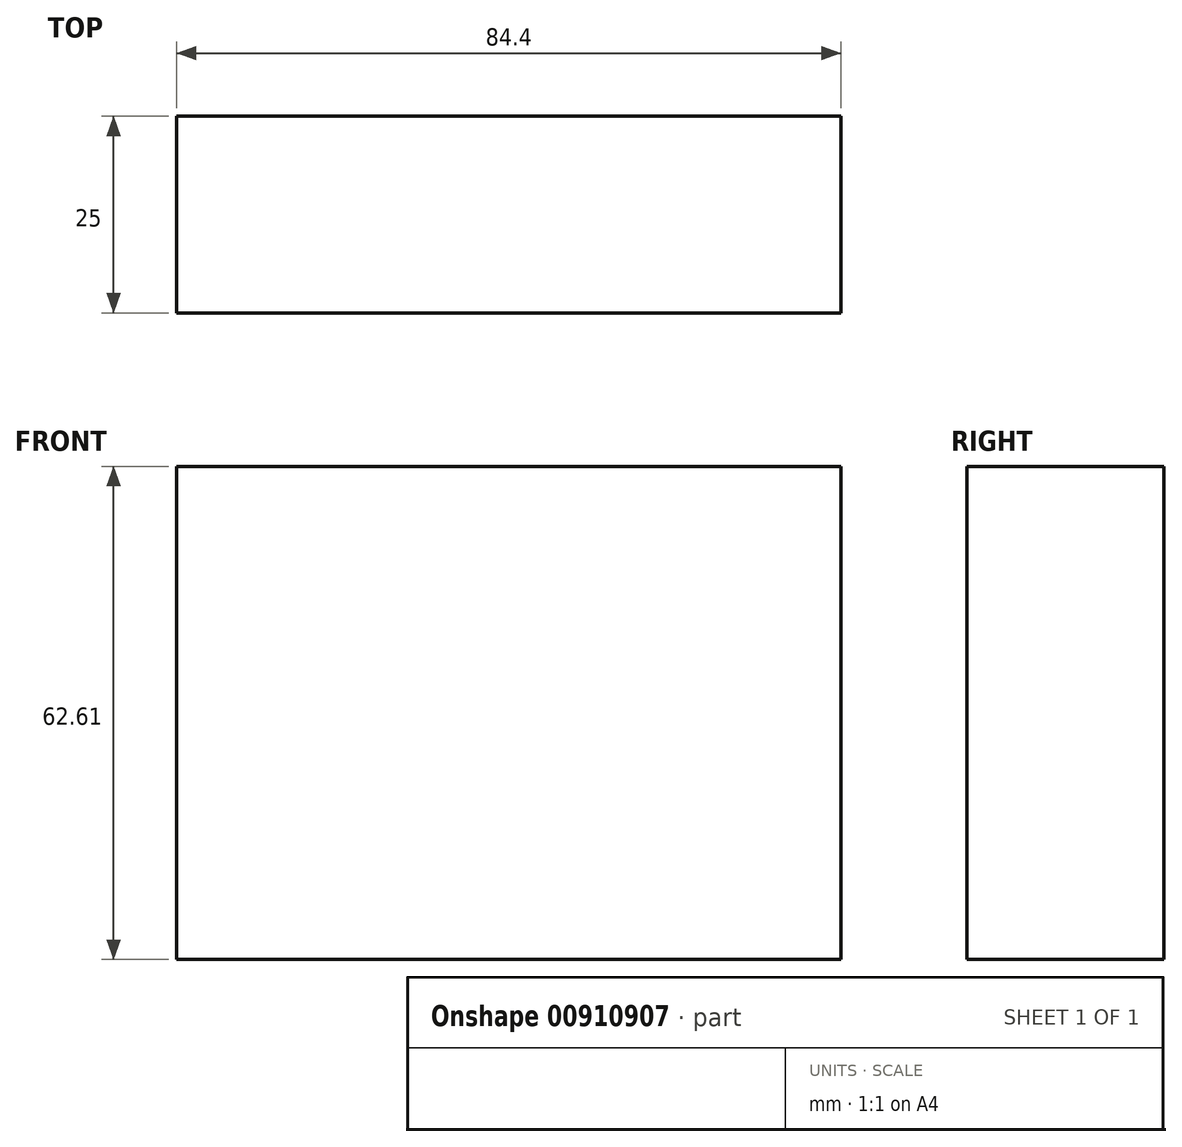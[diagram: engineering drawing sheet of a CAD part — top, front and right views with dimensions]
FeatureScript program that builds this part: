
annotation { "Feature Type Name" : "Feature", "Feature Type Description" : "" }
export const myFeature = defineFeature(function(context is Context, id is Id, definition is map)
    precondition{}
    {
        {
            var Q0;
            Q0=qCreatedBy(makeId("Front.planeOp"),FACE);
            var sketch = newSketch(context, id + "F0", { "sketchPlane" : qUnion([Q0])});
            skLineSegment(sketch, "E0.bottom", {"start": v(-148.41, 22.6) * mm, "end": v(-64.01, 22.6) * mm});
            skLineSegment(sketch, "E0.top", {"start": v(-148.41, -40) * mm, "end": v(-64.01, -40) * mm});
            skLineSegment(sketch, "E0.left", {"start": v(-148.41, 22.6) * mm, "end": v(-148.41, -40) * mm});
            skLineSegment(sketch, "E0.right", {"start": v(-64.01, 22.6) * mm, "end": v(-64.01, -40) * mm});
            skSolve(sketch);
        }
        {
            var Q0;
            Q0 = qSketchRegion(id + "F0", true);
            extrude(context, id + "F1", {"entities" : qUnion([Q0]), "depth" : 25 * mm, "offsetDistance" : 25 * mm});
        }
    });
